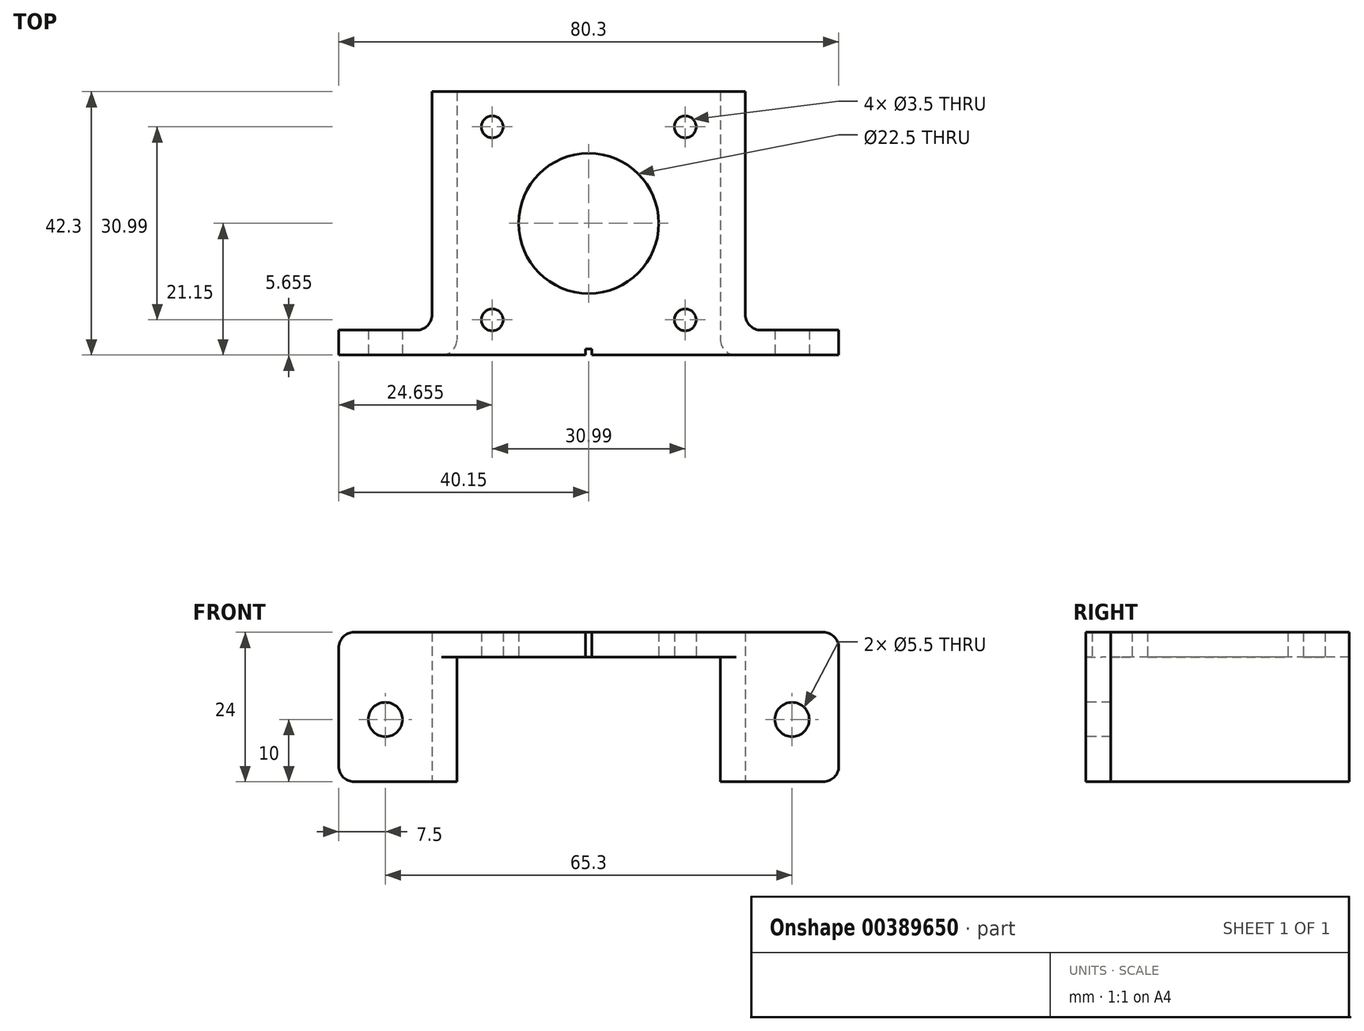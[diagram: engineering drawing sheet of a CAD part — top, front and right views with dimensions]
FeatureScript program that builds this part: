
annotation { "Feature Type Name" : "Feature", "Feature Type Description" : "" }
export const myFeature = defineFeature(function(context is Context, id is Id, definition is map)
    precondition{}
    {
        {
            var Q0;
            Q0=qCreatedBy(makeId("Top.planeOp"),FACE);
            var sketch = newSketch(context, id + "F0", { "sketchPlane" : qUnion([Q0])});
            skLineSegment(sketch, "E0.bottom", {"start": v(-21.15, 21.15) * mm, "end": v(21.15, 21.15) * mm});
            skLineSegment(sketch, "E0.left", {"start": v(-21.15, 21.15) * mm, "end": v(-21.15, -21.15) * mm, "construction": true});
            skLineSegment(sketch, "E0.right", {"start": v(21.15, 21.15) * mm, "end": v(21.15, -21.15) * mm, "construction": true});
            skLineSegment(sketch, "E1.bottom", {"start": v(-15.5, 15.5) * mm, "end": v(15.5, 15.5) * mm, "construction": true});
            skLineSegment(sketch, "E1.top", {"start": v(-15.5, -15.5) * mm, "end": v(15.5, -15.5) * mm, "construction": true});
            skLineSegment(sketch, "E1.left", {"start": v(-15.5, 15.5) * mm, "end": v(-15.5, -15.5) * mm, "construction": true});
            skLineSegment(sketch, "E1.right", {"start": v(15.5, 15.5) * mm, "end": v(15.5, -15.5) * mm, "construction": true});
            skCircle(sketch, "E2", {"center": v(-15.5, 15.5) * mm, "radius": 1.75 * mm});
            skCircle(sketch, "E3", {"center": v(-15.5, -15.5) * mm, "radius": 1.75 * mm});
            skCircle(sketch, "E4", {"center": v(15.5, 15.5) * mm, "radius": 1.75 * mm});
            skCircle(sketch, "E5", {"center": v(15.5, -15.5) * mm, "radius": 1.75 * mm});
            skCircle(sketch, "E6", {"center": v(0, 0) * mm, "radius": 11.25 * mm});
            skLineSegment(sketch, "E7", {"start": v(-21.15, -21.15) * mm, "end": v(21.15, -21.15) * mm});
            skLineSegment(sketch, "E8.bottom", {"start": v(21.15, -21.15) * mm, "end": v(40.15, -21.15) * mm});
            skLineSegment(sketch, "E8.top", {"start": v(21.15, -17.15) * mm, "end": v(40.15, -17.15) * mm});
            skLineSegment(sketch, "E8.left", {"start": v(21.15, -21.15) * mm, "end": v(21.15, -17.15) * mm});
            skLineSegment(sketch, "E8.right", {"start": v(40.15, -21.15) * mm, "end": v(40.15, -17.15) * mm});
            skLineSegment(sketch, "E9.bottom", {"start": v(-21.15, -21.15) * mm, "end": v(-40.15, -21.15) * mm});
            skLineSegment(sketch, "E9.top", {"start": v(-21.15, -17.15) * mm, "end": v(-40.15, -17.15) * mm});
            skLineSegment(sketch, "E9.left", {"start": v(-21.15, -21.15) * mm, "end": v(-21.15, -17.15) * mm});
            skLineSegment(sketch, "E9.right", {"start": v(-40.15, -21.15) * mm, "end": v(-40.15, -17.15) * mm});
            skLineSegment(sketch, "E10.bottom", {"start": v(-21.15, 21.15) * mm, "end": v(-25.15, 21.15) * mm});
            skLineSegment(sketch, "E10.top", {"start": v(-21.15, -17.15) * mm, "end": v(-25.15, -17.15) * mm});
            skLineSegment(sketch, "E10.left", {"start": v(-21.15, 21.15) * mm, "end": v(-21.15, -17.15) * mm});
            skLineSegment(sketch, "E10.right", {"start": v(-25.15, 21.15) * mm, "end": v(-25.15, -17.15) * mm});
            skLineSegment(sketch, "E11.bottom", {"start": v(21.15, 21.15) * mm, "end": v(25.15, 21.15) * mm});
            skLineSegment(sketch, "E11.top", {"start": v(21.15, -17.15) * mm, "end": v(25.15, -17.15) * mm});
            skLineSegment(sketch, "E11.left", {"start": v(21.15, 21.15) * mm, "end": v(21.15, -17.15) * mm});
            skLineSegment(sketch, "E11.right", {"start": v(25.15, 21.15) * mm, "end": v(25.15, -17.15) * mm});
            skSolve(sketch);
        }
        {
            var Q0;
            Q0=qSketchRegion(id+"F0",true);
            extrude(context, id + "F1", {"entities" : qUnion([Q0]), "depth" : 4 * mm});
        }
        {
            var Q0;
            Q0=makeQuery(id+"F1.opExtrude","CAP_FACE",FACE,{"disambiguationData":[OSD([sQuery(id+"F0.wireOp",EDGE,"E0.bottom"),sQuery(id+"F0.wireOp",EDGE,"E2"),sQuery(id+"F0.wireOp",EDGE,"E3"),sQuery(id+"F0.wireOp",EDGE,"E4"),sQuery(id+"F0.wireOp",EDGE,"E5"),sQuery(id+"F0.wireOp",EDGE,"E6"),sQuery(id+"F0.wireOp",EDGE,"E7"),sQuery(id+"F0.wireOp",EDGE,"E8.bottom"),sQuery(id+"F0.wireOp",EDGE,"E8.top"),sQuery(id+"F0.wireOp",EDGE,"E8.right"),sQuery(id+"F0.wireOp",EDGE,"E9.bottom"),sQuery(id+"F0.wireOp",EDGE,"E9.top"),sQuery(id+"F0.wireOp",EDGE,"E9.right"),sQuery(id+"F0.wireOp",EDGE,"E10.bottom"),sQuery(id+"F0.wireOp",EDGE,"E10.right"),sQuery(id+"F0.wireOp",EDGE,"E11.bottom"),sQuery(id+"F0.wireOp",EDGE,"E11.right")])],"isStart":true});
            var sketch = newSketch(context, id + "F2", { "sketchPlane" : qUnion([Q0])});
            skLineSegment(sketch, "E12.0", {"start": v(-21.15, -21.15) * mm, "end": v(-21.15, 17.15) * mm});
            skLineSegment(sketch, "E13.0", {"start": v(-21.15, 21.15) * mm, "end": v(-21.15, 17.15) * mm});
            skLineSegment(sketch, "E14.0", {"start": v(-21.15, 21.15) * mm, "end": v(-40.15, 21.15) * mm});
            skLineSegment(sketch, "E15.0", {"start": v(-40.15, 21.15) * mm, "end": v(-40.15, 17.15) * mm});
            skLineSegment(sketch, "E16.0", {"start": v(-25.15, -21.15) * mm, "end": v(-25.15, 17.15) * mm});
            skLineSegment(sketch, "E17.0", {"start": v(-25.15, 17.15) * mm, "end": v(-40.15, 17.15) * mm});
            skLineSegment(sketch, "E18.0", {"start": v(-21.15, -21.15) * mm, "end": v(-25.15, -21.15) * mm});
            skLineSegment(sketch, "E19.0", {"start": v(21.15, -21.15) * mm, "end": v(25.15, -21.15) * mm});
            skLineSegment(sketch, "E20.0", {"start": v(21.15, -21.15) * mm, "end": v(21.15, 17.15) * mm});
            skLineSegment(sketch, "E21.0", {"start": v(25.15, -21.15) * mm, "end": v(25.15, 17.15) * mm});
            skLineSegment(sketch, "E22.0", {"start": v(25.15, 17.15) * mm, "end": v(40.15, 17.15) * mm});
            skLineSegment(sketch, "E23.0", {"start": v(40.15, 21.15) * mm, "end": v(40.15, 17.15) * mm});
            skLineSegment(sketch, "E24.0", {"start": v(21.15, 21.15) * mm, "end": v(40.15, 21.15) * mm});
            skLineSegment(sketch, "E25.0", {"start": v(21.15, 21.15) * mm, "end": v(21.15, 17.15) * mm});
            skPoint(sketch, "E26.orphan", {"position": v(-21.15, 17.15) * mm});
            skPoint(sketch, "E27.orphan", {"position": v(21.15, 17.15) * mm});
            skSolve(sketch);
        }
        {
            var Q0;
            Q0=qSketchRegion(id+"F2",true);
            extrude(context, id + "F3", {"entities" : qUnion([Q0]), "operationType" : NewBodyOperationType.ADD, "depth" : 20 * mm});
        }
        {
            var Q0;
            Q0=makeQuery(id+"F3.boolean.opBoolean","MERGE",FACE,{"derivedFrom":[makeQuery(id+"F1.opExtrude","SWEPT_FACE",FACE,{"disambiguationData":[OSD([sQuery(id+"F0.wireOp",EDGE,"E7"),sQuery(id+"F0.wireOp",EDGE,"E8.bottom"),sQuery(id+"F0.wireOp",EDGE,"E9.bottom")])]}),makeQuery(id+"F3.opExtrude","SWEPT_FACE",FACE,{"disambiguationData":[OSD([sQuery(id+"F2.wireOp",EDGE,"E14.0")])]}),makeQuery(id+"F3.opExtrude","SWEPT_FACE",FACE,{"disambiguationData":[OSD([sQuery(id+"F2.wireOp",EDGE,"E24.0")])]})]});
            var sketch = newSketch(context, id + "F4", { "sketchPlane" : qUnion([Q0])});
            skCircle(sketch, "E28", {"center": v(-32.65, -10) * mm, "radius": 2.75 * mm});
            skPoint(sketch, "E28.centerSnap1", {"position": v(-21.15, -10) * mm});
            skCircle(sketch, "E29", {"center": v(32.65, -10) * mm, "radius": 2.75 * mm});
            skPoint(sketch, "E29.centerSnap0", {"position": v(21.15, -10) * mm});
            skSolve(sketch);
        }
        {
            var Q0;
            Q0=qSketchRegion(id+"F4",true);
            extrude(context, id + "F5", {"entities" : qUnion([Q0]), "operationType" : NewBodyOperationType.REMOVE, "endBound" : BoundingType.UP_TO_NEXT, "oppositeDirection" : true, "depth" : 25 * mm});
        }
        {
            var Q0;
            Q0=makeQuery(id+"F1.opExtrude","CAP_EDGE",EDGE,{"disambiguationData":[OSD([sQuery(id+"F0.wireOp",EDGE,"E9.right")])],"isStart":false});
            var Q1;
            Q1=makeQuery(id+"F3.opExtrude","CAP_EDGE",EDGE,{"disambiguationData":[OSD([sQuery(id+"F2.wireOp",EDGE,"E15.0")])],"isStart":false});
            var Q2;
            Q2=makeQuery(id+"F3.opExtrude","CAP_EDGE",EDGE,{"disambiguationData":[OSD([sQuery(id+"F2.wireOp",EDGE,"E23.0")])],"isStart":false});
            var Q3;
            Q3=makeQuery(id+"F1.opExtrude","CAP_EDGE",EDGE,{"disambiguationData":[OSD([sQuery(id+"F0.wireOp",EDGE,"E8.right")])],"isStart":false});
            var Q4;
            Q4=makeQuery(id+"F3.boolean.opBoolean","MERGE",EDGE,{"derivedFrom":[makeQuery(id+"F1.opExtrude","SWEPT_EDGE",EDGE,{"disambiguationData":[OSD([sQuery(id+"F0.wireOp",EDGE,"E8.top"),sQuery(id+"F0.wireOp",EDGE,"E11.top"),sQuery(id+"F0.wireOp",EDGE,"E11.right")])]}),makeQuery(id+"F3.opExtrude","SWEPT_EDGE",EDGE,{"disambiguationData":[OSD([sQuery(id+"F2.wireOp",EDGE,"E21.0"),sQuery(id+"F2.wireOp",EDGE,"E22.0")])]})]});
            var Q5;
            Q5=makeQuery(id+"F3.boolean.opBoolean","MERGE",EDGE,{"derivedFrom":[makeQuery(id+"F1.opExtrude","SWEPT_EDGE",EDGE,{"disambiguationData":[OSD([sQuery(id+"F0.wireOp",EDGE,"E9.top"),sQuery(id+"F0.wireOp",EDGE,"E10.top"),sQuery(id+"F0.wireOp",EDGE,"E10.right")])]}),makeQuery(id+"F3.opExtrude","SWEPT_EDGE",EDGE,{"disambiguationData":[OSD([sQuery(id+"F2.wireOp",EDGE,"E16.0"),sQuery(id+"F2.wireOp",EDGE,"E17.0")])]})]});
            var Q6;
            Q6=makeQuery(id+"F3.opExtrude","SWEPT_EDGE",EDGE,{"disambiguationData":[OSD([sQuery(id+"F0.wireOp",EDGE,"E7"),sQuery(id+"F0.wireOp",EDGE,"E8.bottom"),sQuery(id+"F0.wireOp",EDGE,"E9.bottom"),sQuery(id+"F2.wireOp",EDGE,"E24.0"),sQuery(id+"F2.wireOp",EDGE,"E25.0")])]});
            var Q7;
            Q7=makeQuery(id+"F3.opExtrude","SWEPT_EDGE",EDGE,{"disambiguationData":[OSD([sQuery(id+"F0.wireOp",EDGE,"E7"),sQuery(id+"F0.wireOp",EDGE,"E8.bottom"),sQuery(id+"F0.wireOp",EDGE,"E9.bottom"),sQuery(id+"F2.wireOp",EDGE,"E13.0"),sQuery(id+"F2.wireOp",EDGE,"E14.0")])]});
            fillet(context, id + "F6", {"entities" : qUnion([Q0, Q1, Q2, Q3, Q4, Q5, Q6, Q7]), "radius" : 2.5 * mm, "tangentPropagation" : true, "allowEdgeOverflow" : false});
        }
        {
            var Q0;
            Q0=makeQuery(id+"F3.boolean.opBoolean","MERGE",FACE,{"derivedFrom":[makeQuery(id+"F1.opExtrude","SWEPT_FACE",FACE,{"disambiguationData":[OSD([sQuery(id+"F0.wireOp",EDGE,"E7"),sQuery(id+"F0.wireOp",EDGE,"E8.bottom"),sQuery(id+"F0.wireOp",EDGE,"E9.bottom")])]}),makeQuery(id+"F3.opExtrude","SWEPT_FACE",FACE,{"disambiguationData":[OSD([sQuery(id+"F2.wireOp",EDGE,"E14.0")])]}),makeQuery(id+"F3.opExtrude","SWEPT_FACE",FACE,{"disambiguationData":[OSD([sQuery(id+"F2.wireOp",EDGE,"E24.0")])]})]});
            var sketch = newSketch(context, id + "F7", { "sketchPlane" : qUnion([Q0])});
            skLineSegment(sketch, "E30.bottom", {"start": v(0, 4) * mm, "end": v(0.5, 4) * mm});
            skLineSegment(sketch, "E30.top", {"start": v(0, 0) * mm, "end": v(0.5, 0) * mm});
            skLineSegment(sketch, "E30.left", {"start": v(0, 4) * mm, "end": v(0, 0) * mm});
            skLineSegment(sketch, "E30.right", {"start": v(0.5, 4) * mm, "end": v(0.5, 0) * mm});
            skLineSegment(sketch, "E31.MirrorCS", {"start": v(-0.5, 4) * mm, "end": v(-0.5, 0) * mm});
            skLineSegment(sketch, "E32.MirrorCS", {"start": v(0, 0) * mm, "end": v(-0.5, 0) * mm});
            skLineSegment(sketch, "E33.MirrorCS", {"start": v(0, 4) * mm, "end": v(-0.5, 4) * mm});
            skSolve(sketch);
        }
        {
            var Q0;
            Q0=qSketchRegion(id+"F7",true);
            extrude(context, id + "F8", {"entities" : qUnion([Q0]), "operationType" : NewBodyOperationType.REMOVE, "oppositeDirection" : true, "depth" : 1 * mm});
        }
    });
